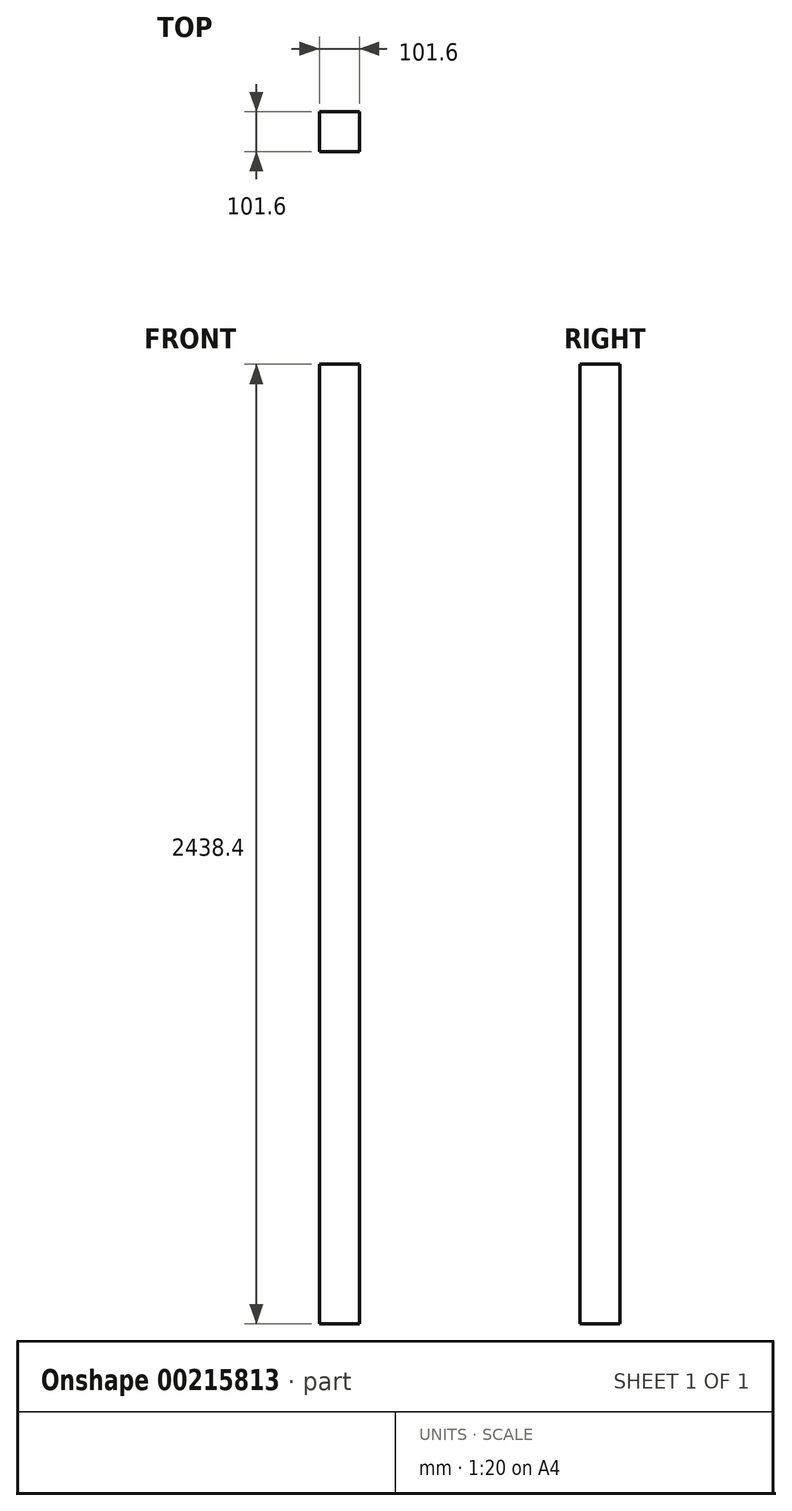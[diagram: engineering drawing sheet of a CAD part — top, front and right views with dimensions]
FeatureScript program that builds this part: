
annotation { "Feature Type Name" : "Feature", "Feature Type Description" : "" }
export const myFeature = defineFeature(function(context is Context, id is Id, definition is map)
    precondition{}
    {
        {
            var Q0;
            Q0=qCreatedBy(makeId("Top.planeOp"),FACE);
            var sketch = newSketch(context, id + "F0", { "sketchPlane" : qUnion([Q0])});
            skLineSegment(sketch, "E0.bottom", {"start": v(-50.8, 50.8) * mm, "end": v(50.8, 50.8) * mm});
            skLineSegment(sketch, "E0.top", {"start": v(-50.8, -50.8) * mm, "end": v(50.8, -50.8) * mm});
            skLineSegment(sketch, "E0.left", {"start": v(-50.8, 50.8) * mm, "end": v(-50.8, -50.8) * mm});
            skLineSegment(sketch, "E0.right", {"start": v(50.8, 50.8) * mm, "end": v(50.8, -50.8) * mm});
            skSolve(sketch);
        }
        {
            var Q0;
            Q0 = qSketchRegion(id + "F0", true);
            extrude(context, id + "F1", {"entities" : qUnion([Q0]), "depth" : 2438.4 * mm});
        }
    });
